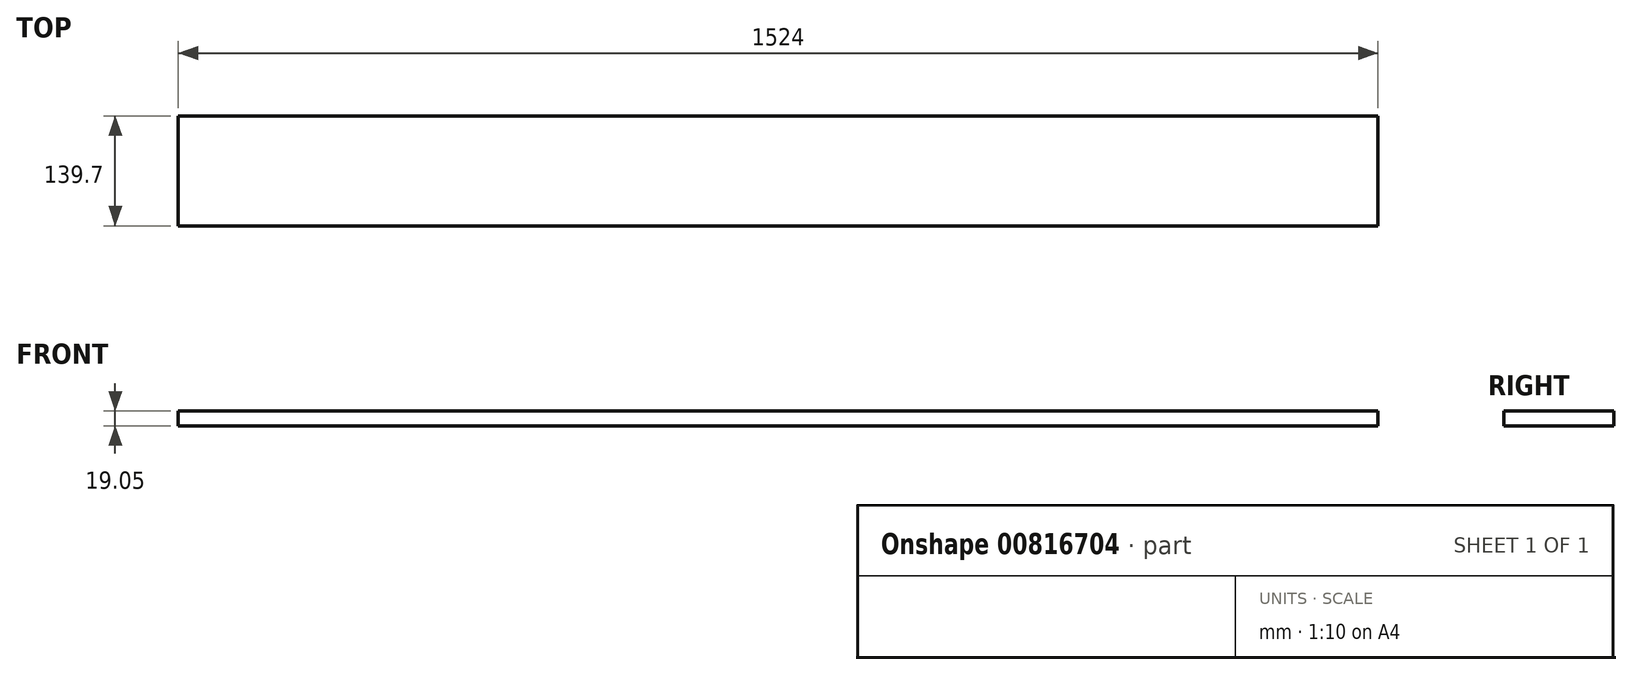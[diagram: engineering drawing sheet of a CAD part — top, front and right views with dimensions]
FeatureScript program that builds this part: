
annotation { "Feature Type Name" : "Feature", "Feature Type Description" : "" }
export const myFeature = defineFeature(function(context is Context, id is Id, definition is map)
    precondition{}
    {
        {
            var Q0;
            Q0=qCreatedBy(makeId("Top.planeOp"),FACE);
            var sketch = newSketch(context, id + "F0", { "sketchPlane" : qUnion([Q0])});
            skLineSegment(sketch, "E0.bottom", {"start": v(0, 0) * mm, "end": v(1524, 0) * mm});
            skLineSegment(sketch, "E0.top", {"start": v(0, 139.7) * mm, "end": v(1524, 139.7) * mm});
            skLineSegment(sketch, "E0.left", {"start": v(0, 0) * mm, "end": v(0, 139.7) * mm});
            skLineSegment(sketch, "E0.right", {"start": v(1524, 0) * mm, "end": v(1524, 139.7) * mm});
            skSolve(sketch);
        }
        {
            var Q0;
            Q0 = qSketchRegion(id + "F0", true);
            extrude(context, id + "F1", {"entities" : qUnion([Q0]), "depth" : 19.05 * mm, "offsetDistance" : 25.4 * mm});
        }
    });
